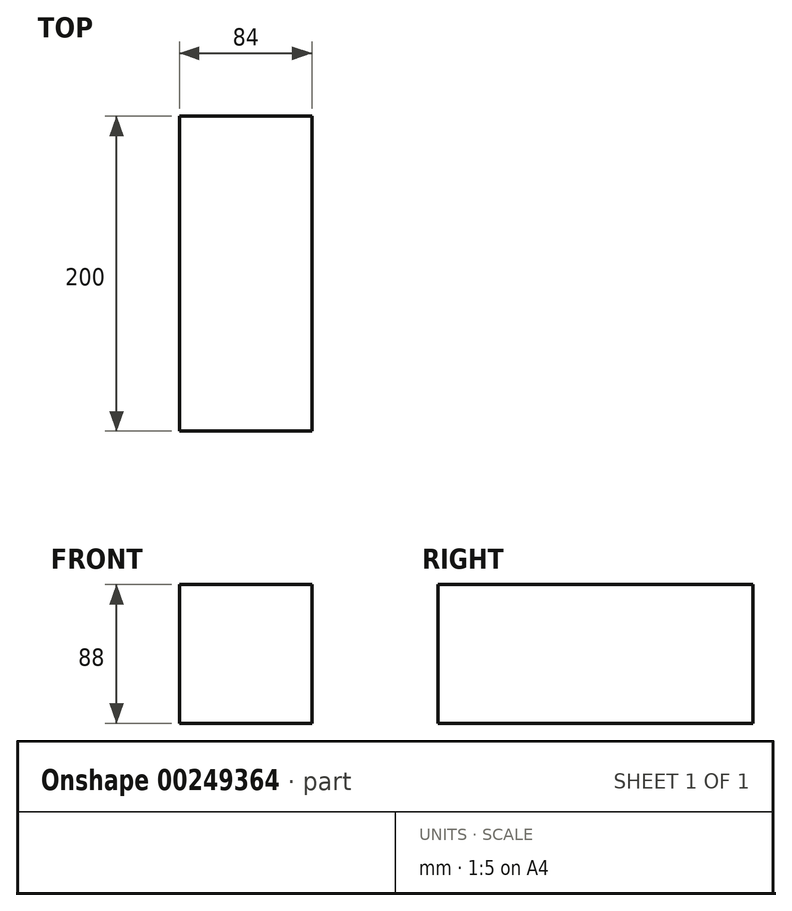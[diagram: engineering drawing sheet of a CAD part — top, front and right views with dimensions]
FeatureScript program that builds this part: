
annotation { "Feature Type Name" : "Feature", "Feature Type Description" : "" }
export const myFeature = defineFeature(function(context is Context, id is Id, definition is map)
    precondition{}
    {
        {
            var Q0;
            Q0=qCreatedBy(makeId("Front.planeOp"),FACE);
            var sketch = newSketch(context, id + "F0", { "sketchPlane" : qUnion([Q0])});
            skLineSegment(sketch, "E0.bottom", {"start": v(42, 44) * mm, "end": v(-42, 44) * mm});
            skLineSegment(sketch, "E0.top", {"start": v(42, -44) * mm, "end": v(-42, -44) * mm});
            skLineSegment(sketch, "E0.left", {"start": v(42, 44) * mm, "end": v(42, -44) * mm});
            skLineSegment(sketch, "E0.right", {"start": v(-42, 44) * mm, "end": v(-42, -44) * mm});
            skSolve(sketch);
        }
        {
            var Q0;
            Q0=makeQuery(id+"F0.imprint","IMPRINT",FACE,{"disambiguationData":[TD([[makeQuery(id+"F0.imprint","IMPRINT",EDGE,{"derivedFrom":sQuery(id+"F0.wireOp",EDGE,"E0.bottom")}),1.0]])]});
            extrude(context, id + "F1", {"entities" : qUnion([Q0]), "depth" : 200 * mm});
        }
    });
